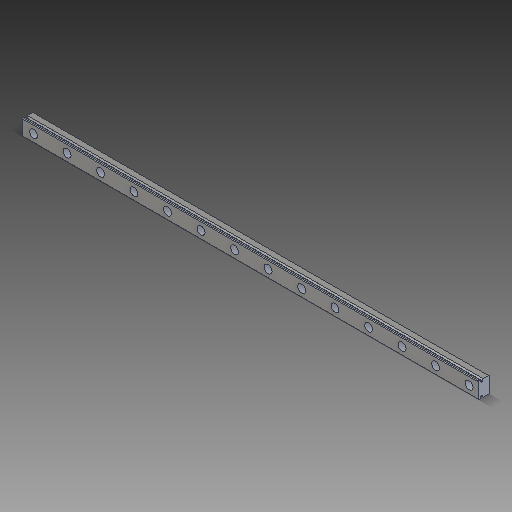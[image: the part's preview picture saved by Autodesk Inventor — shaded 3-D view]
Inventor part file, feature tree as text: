
AUTODESK INVENTOR PART (.ipt)
format: ipt  version: 2017.3 (Build 213256000, 256)  size: 219,136 bytes
history: native  units: mm
features: extrude x2, sketch x2, fillet x1
ambient origin geometry x8: Origin, YZ Plane, XZ Plane, XY Plane, X Axis, Y Axis, Z Axis, Center Point
bodies: Solid1 (feature_tree)
feature tree (5):
  extrude  "Extrusion3"  Depth=12.0mm
  extrude  "Extrusion4"  Depth=12.0mm
  sketch  "Sketch1"  dims[d0=12.0mm d1=9.0mm]
  fillet  "Fillet1"  Radius=30.0mm
  sketch  "Sketch3"  dims[d8=30.0mm d9=0.0mm d10=12.0mm d11=9.0mm d12=30.0mm d13=0.0mm]
